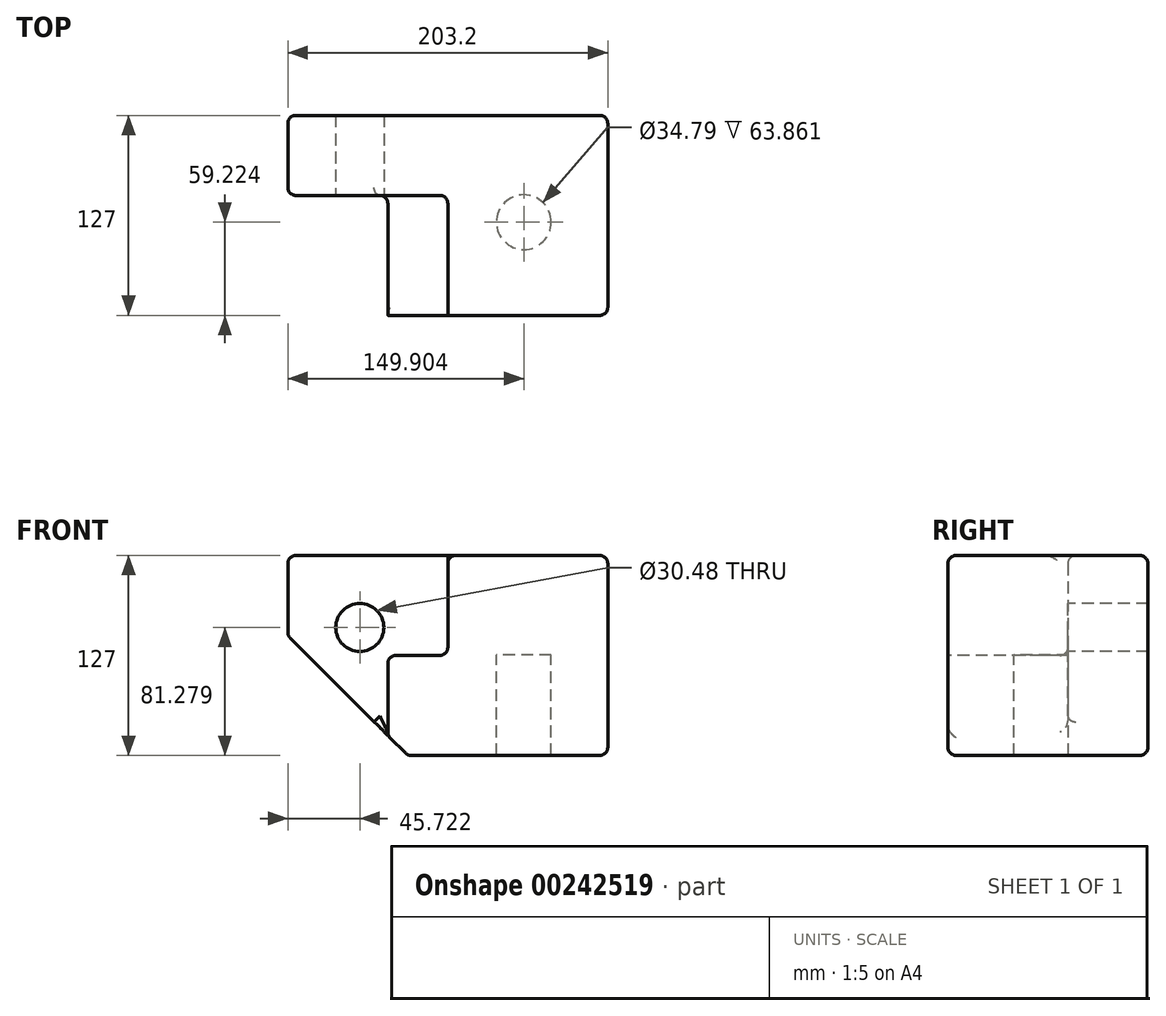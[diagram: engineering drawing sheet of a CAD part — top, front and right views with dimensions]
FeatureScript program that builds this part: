
annotation { "Feature Type Name" : "Feature", "Feature Type Description" : "" }
export const myFeature = defineFeature(function(context is Context, id is Id, definition is map)
    precondition{}
    {
        {
            var Q0;
            Q0=qCreatedBy(makeId("Front.planeOp"),FACE);
            var sketch = newSketch(context, id + "F0", { "sketchPlane" : qUnion([Q0])});
            skLineSegment(sketch, "E0.bottom", {"start": v(-79.8, 63.14) * mm, "end": v(123.4, 63.14) * mm});
            skLineSegment(sketch, "E0.top", {"start": v(-79.8, -63.86) * mm, "end": v(123.4, -63.86) * mm});
            skLineSegment(sketch, "E0.left", {"start": v(-79.8, 63.14) * mm, "end": v(-79.8, -63.86) * mm});
            skLineSegment(sketch, "E0.right", {"start": v(123.4, 63.14) * mm, "end": v(123.4, -63.86) * mm});
            skSolve(sketch);
        }
        {
            var Q0;
            Q0=makeQuery(id+"F0.imprint","IMPRINT",FACE,{"disambiguationData":[TD([[makeQuery(id+"F0.imprint","IMPRINT",EDGE,{"derivedFrom":sQuery(id+"F0.wireOp",EDGE,"E0.bottom")}),-1.0]])]});
            extrude(context, id + "F1", {"entities" : qUnion([Q0]), "depth" : 127 * mm});
        }
        {
            var Q0;
            Q0=makeQuery(id+"F1.opExtrude","CAP_FACE",FACE,{"disambiguationData":[OSD([sQuery(id+"F0.wireOp",EDGE,"E0.bottom"),sQuery(id+"F0.wireOp",EDGE,"E0.top"),sQuery(id+"F0.wireOp",EDGE,"E0.left"),sQuery(id+"F0.wireOp",EDGE,"E0.right")])],"isStart":false});
            var sketch = newSketch(context, id + "F2", { "sketchPlane" : qUnion([Q0])});
            skLineSegment(sketch, "E1", {"start": v(-79.8, 63.14) * mm, "end": v(21.8, 63.14) * mm});
            skLineSegment(sketch, "E2", {"start": v(21.8, 63.14) * mm, "end": v(21.8, -0.36) * mm});
            skLineSegment(sketch, "E3", {"start": v(21.8, -0.36) * mm, "end": v(-16.3, -0.36) * mm});
            skLineSegment(sketch, "E4", {"start": v(-16.3, -0.36) * mm, "end": v(-16.3, -63.86) * mm});
            skLineSegment(sketch, "E5", {"start": v(-16.3, -63.86) * mm, "end": v(-79.8, -63.86) * mm});
            skLineSegment(sketch, "E6", {"start": v(-79.8, -63.86) * mm, "end": v(-79.8, 63.14) * mm});
            skSolve(sketch);
        }
        {
            var Q0;
            Q0=makeQuery(id+"F2.imprint","IMPRINT",FACE,{"disambiguationData":[TD([[makeQuery(id+"F2.imprint","IMPRINT",EDGE,{"derivedFrom":sQuery(id+"F2.wireOp",EDGE,"E1")}),-1.0]])]});
            extrude(context, id + "F3", {"entities" : qUnion([Q0]), "operationType" : NewBodyOperationType.REMOVE, "oppositeDirection" : true, "depth" : 76.2 * mm});
        }
        {
            var Q0;
            Q0=makeQuery(id+"F1.opExtrude","SWEPT_EDGE",EDGE,{"disambiguationData":[OSD([sQuery(id+"F0.wireOp",EDGE,"E0.top"),sQuery(id+"F0.wireOp",EDGE,"E0.left")])]});
            chamfer(context, id + "F4", {"entities" : qUnion([Q0]), "chamferType" : ChamferType.TWO_OFFSETS, "width1" : 76.2 * mm, "oppositeDirection" : false, "width2" : 76.2 * mm, "tangentPropagation" : true});
        }
        {
            var Q0;
            Q0=makeQuery(id+"F1.opExtrude","CAP_EDGE",EDGE,{"disambiguationData":[OSD([sQuery(id+"F0.wireOp",EDGE,"E0.top")])],"isStart":false});
            var Q1;
            {var subQ0=sQuery(id+"F0.wireOp",EDGE,"E0.top");Q1=makeQuery(id+"F4.opChamfer","BLEND_EDGE",EDGE,{"blendedFrom":[makeQuery(id+"F1.opExtrude","SWEPT_EDGE",EDGE,{"disambiguationData":[OSD([subQ0,sQuery(id+"F0.wireOp",EDGE,"E0.left")])]}),makeQuery(id+"F1.opExtrude","SWEPT_FACE",FACE,{"disambiguationData":[OSD([subQ0])]})],"blendedInto":[makeQuery(id+"F1.opExtrude","SWEPT_FACE",FACE,{"disambiguationData":[OSD([subQ0])]})]});}
            var Q2;
            {var subQ0=sQuery(id+"F0.wireOp",EDGE,"E0.left");var subQ1=sQuery(id+"F0.wireOp",EDGE,"E0.top");Q2=makeQuery(id+"F4.opChamfer","BLEND_EDGE",EDGE,{"blendedFrom":[makeQuery(id+"F1.opExtrude","SWEPT_EDGE",EDGE,{"disambiguationData":[OSD([subQ1,subQ0])]}),makeQuery(id+"F1.opExtrude","CAP_FACE",FACE,{"disambiguationData":[OSD([sQuery(id+"F0.wireOp",EDGE,"E0.bottom"),subQ1,subQ0,sQuery(id+"F0.wireOp",EDGE,"E0.right")])],"isStart":false})],"blendedInto":[makeQuery(id+"F1.opExtrude","CAP_FACE",FACE,{"disambiguationData":[OSD([sQuery(id+"F0.wireOp",EDGE,"E0.bottom"),subQ1,subQ0,sQuery(id+"F0.wireOp",EDGE,"E0.right")])],"isStart":false})]});}
            var Q3;
            Q3=makeQuery(id+"F4.opChamfer","BLEND_EDGE",EDGE,{"blendedFrom":[makeQuery(id+"F1.opExtrude","SWEPT_EDGE",EDGE,{"disambiguationData":[OSD([sQuery(id+"F0.wireOp",EDGE,"E0.top"),sQuery(id+"F0.wireOp",EDGE,"E0.left")])]}),makeQuery(id+"F3.boolean.opBoolean","COPY",FACE,{"derivedFrom":makeQuery(id+"F3.opExtrude","SWEPT_FACE",FACE,{"disambiguationData":[OSD([sQuery(id+"F2.wireOp",EDGE,"E4")])]})})],"blendedInto":[makeQuery(id+"F3.boolean.opBoolean","COPY",FACE,{"derivedFrom":makeQuery(id+"F3.opExtrude","SWEPT_FACE",FACE,{"disambiguationData":[OSD([sQuery(id+"F2.wireOp",EDGE,"E4")])]})})]});
            var Q4;
            Q4=makeQuery(id+"F4.opChamfer","BLEND_EDGE",EDGE,{"blendedFrom":[makeQuery(id+"F1.opExtrude","SWEPT_EDGE",EDGE,{"disambiguationData":[OSD([sQuery(id+"F0.wireOp",EDGE,"E0.top"),sQuery(id+"F0.wireOp",EDGE,"E0.left")])]}),makeQuery(id+"F3.boolean.opBoolean","COPY",FACE,{"derivedFrom":makeQuery(id+"F3.opExtrude","CAP_FACE",FACE,{"disambiguationData":[OSD([sQuery(id+"F2.wireOp",EDGE,"E1"),sQuery(id+"F2.wireOp",EDGE,"E2"),sQuery(id+"F2.wireOp",EDGE,"E3"),sQuery(id+"F2.wireOp",EDGE,"E4"),sQuery(id+"F2.wireOp",EDGE,"E5"),sQuery(id+"F2.wireOp",EDGE,"E6")])],"isStart":false})})],"blendedInto":[makeQuery(id+"F3.boolean.opBoolean","COPY",FACE,{"derivedFrom":makeQuery(id+"F3.opExtrude","CAP_FACE",FACE,{"disambiguationData":[OSD([sQuery(id+"F2.wireOp",EDGE,"E1"),sQuery(id+"F2.wireOp",EDGE,"E2"),sQuery(id+"F2.wireOp",EDGE,"E3"),sQuery(id+"F2.wireOp",EDGE,"E4"),sQuery(id+"F2.wireOp",EDGE,"E5"),sQuery(id+"F2.wireOp",EDGE,"E6")])],"isStart":false})})]});
            var Q5;
            {var subQ0=sQuery(id+"F0.wireOp",EDGE,"E0.left");var subQ1=sQuery(id+"F0.wireOp",EDGE,"E0.top");Q5=makeQuery(id+"F4.opChamfer","BLEND_EDGE",EDGE,{"blendedFrom":[makeQuery(id+"F1.opExtrude","SWEPT_EDGE",EDGE,{"disambiguationData":[OSD([subQ1,subQ0])]}),makeQuery(id+"F1.opExtrude","CAP_FACE",FACE,{"disambiguationData":[OSD([sQuery(id+"F0.wireOp",EDGE,"E0.bottom"),subQ1,subQ0,sQuery(id+"F0.wireOp",EDGE,"E0.right")])],"isStart":true})],"blendedInto":[makeQuery(id+"F1.opExtrude","CAP_FACE",FACE,{"disambiguationData":[OSD([sQuery(id+"F0.wireOp",EDGE,"E0.bottom"),subQ1,subQ0,sQuery(id+"F0.wireOp",EDGE,"E0.right")])],"isStart":true})]});}
            var Q6;
            {var subQ0=sQuery(id+"F0.wireOp",EDGE,"E0.left");Q6=makeQuery(id+"F4.opChamfer","BLEND_EDGE",EDGE,{"blendedFrom":[makeQuery(id+"F1.opExtrude","SWEPT_EDGE",EDGE,{"disambiguationData":[OSD([sQuery(id+"F0.wireOp",EDGE,"E0.top"),subQ0])]}),makeQuery(id+"F1.opExtrude","SWEPT_FACE",FACE,{"disambiguationData":[OSD([subQ0])]})],"blendedInto":[makeQuery(id+"F1.opExtrude","SWEPT_FACE",FACE,{"disambiguationData":[OSD([subQ0])]})]});}
            var Q7;
            Q7=makeQuery(id+"F3.boolean.opBoolean","COPY",EDGE,{"derivedFrom":makeQuery(id+"F3.opExtrude","SWEPT_EDGE",EDGE,{"disambiguationData":[OSD([sQuery(id+"F2.wireOp",EDGE,"E3"),sQuery(id+"F2.wireOp",EDGE,"E4")])]})});
            var Q8;
            Q8=makeQuery(id+"F3.boolean.opBoolean","COPY",EDGE,{"derivedFrom":makeQuery(id+"F3.opExtrude","CAP_EDGE",EDGE,{"disambiguationData":[OSD([sQuery(id+"F2.wireOp",EDGE,"E4")])],"isStart":true})});
            var Q9;
            Q9=makeQuery(id+"F3.boolean.opBoolean","COPY",EDGE,{"derivedFrom":makeQuery(id+"F3.opExtrude","CAP_EDGE",EDGE,{"disambiguationData":[OSD([sQuery(id+"F2.wireOp",EDGE,"E4")])],"isStart":false})});
            var Q10;
            Q10=makeQuery(id+"F3.boolean.opBoolean","COPY",FACE,{"derivedFrom":makeQuery(id+"F3.opExtrude","CAP_FACE",FACE,{"disambiguationData":[OSD([sQuery(id+"F2.wireOp",EDGE,"E1"),sQuery(id+"F2.wireOp",EDGE,"E2"),sQuery(id+"F2.wireOp",EDGE,"E3"),sQuery(id+"F2.wireOp",EDGE,"E4"),sQuery(id+"F2.wireOp",EDGE,"E5"),sQuery(id+"F2.wireOp",EDGE,"E6")])],"isStart":false})});
            var Q11;
            Q11=makeQuery(id+"F3.boolean.opBoolean","COPY",EDGE,{"derivedFrom":makeQuery(id+"F3.opExtrude","CAP_EDGE",EDGE,{"disambiguationData":[OSD([sQuery(id+"F2.wireOp",EDGE,"E6")])],"isStart":false})});
            var Q12;
            Q12=makeQuery(id+"F1.opExtrude","CAP_EDGE",EDGE,{"disambiguationData":[OSD([sQuery(id+"F0.wireOp",EDGE,"E0.left")])],"isStart":true});
            var Q13;
            Q13=makeQuery(id+"F1.opExtrude","SWEPT_EDGE",EDGE,{"disambiguationData":[OSD([sQuery(id+"F0.wireOp",EDGE,"E0.bottom"),sQuery(id+"F0.wireOp",EDGE,"E0.left")])]});
            var Q14;
            Q14=makeQuery(id+"F1.opExtrude","CAP_EDGE",EDGE,{"disambiguationData":[OSD([sQuery(id+"F0.wireOp",EDGE,"E0.bottom")])],"isStart":false});
            var Q15;
            Q15=makeQuery(id+"F1.opExtrude","CAP_EDGE",EDGE,{"disambiguationData":[OSD([sQuery(id+"F0.wireOp",EDGE,"E0.right")])],"isStart":false});
            var Q16;
            Q16=makeQuery(id+"F1.opExtrude","SWEPT_EDGE",EDGE,{"disambiguationData":[OSD([sQuery(id+"F0.wireOp",EDGE,"E0.top"),sQuery(id+"F0.wireOp",EDGE,"E0.right")])]});
            var Q17;
            Q17=makeQuery(id+"F1.opExtrude","CAP_EDGE",EDGE,{"disambiguationData":[OSD([sQuery(id+"F0.wireOp",EDGE,"E0.top")])],"isStart":true});
            var Q18;
            Q18=makeQuery(id+"F1.opExtrude","CAP_EDGE",EDGE,{"disambiguationData":[OSD([sQuery(id+"F0.wireOp",EDGE,"E0.bottom")])],"isStart":true});
            var Q19;
            Q19=makeQuery(id+"F1.opExtrude","CAP_EDGE",EDGE,{"disambiguationData":[OSD([sQuery(id+"F0.wireOp",EDGE,"E0.right")])],"isStart":true});
            var Q20;
            Q20=makeQuery(id+"F1.opExtrude","SWEPT_EDGE",EDGE,{"disambiguationData":[OSD([sQuery(id+"F0.wireOp",EDGE,"E0.bottom"),sQuery(id+"F0.wireOp",EDGE,"E0.right")])]});
            var Q21;
            Q21=makeQuery(id+"F3.boolean.opBoolean","COPY",EDGE,{"derivedFrom":makeQuery(id+"F3.opExtrude","CAP_EDGE",EDGE,{"disambiguationData":[OSD([sQuery(id+"F2.wireOp",EDGE,"E2")])],"isStart":true})});
            var Q22;
            Q22=makeQuery(id+"F3.boolean.opBoolean","COPY",EDGE,{"derivedFrom":makeQuery(id+"F3.opExtrude","CAP_EDGE",EDGE,{"disambiguationData":[OSD([sQuery(id+"F2.wireOp",EDGE,"E3")])],"isStart":true})});
            var Q23;
            Q23=makeQuery(id+"F3.boolean.opBoolean","COPY",EDGE,{"derivedFrom":makeQuery(id+"F3.opExtrude","SWEPT_EDGE",EDGE,{"disambiguationData":[OSD([sQuery(id+"F2.wireOp",EDGE,"E2"),sQuery(id+"F2.wireOp",EDGE,"E3")])]})});
            fillet(context, id + "F5", {"entities" : qUnion([Q0, Q1, Q2, Q3, Q4, Q5, Q6, Q7, Q8, Q9, Q10, Q11, Q12, Q13, Q14, Q15, Q16, Q17, Q18, Q19, Q20, Q21, Q22, Q23]), "radius" : 5.08 * mm, "tangentPropagation" : true, "allowEdgeOverflow" : false});
        }
        {
            var Q0;
            Q0=makeQuery(id+"F3.boolean.opBoolean","COPY",FACE,{"derivedFrom":makeQuery(id+"F3.opExtrude","CAP_FACE",FACE,{"disambiguationData":[OSD([sQuery(id+"F2.wireOp",EDGE,"E1"),sQuery(id+"F2.wireOp",EDGE,"E2"),sQuery(id+"F2.wireOp",EDGE,"E3"),sQuery(id+"F2.wireOp",EDGE,"E4"),sQuery(id+"F2.wireOp",EDGE,"E5"),sQuery(id+"F2.wireOp",EDGE,"E6")])],"isStart":false})});
            var sketch = newSketch(context, id + "F6", { "sketchPlane" : qUnion([Q0])});
            skCircle(sketch, "E7", {"center": v(-34.09, 17.42) * mm, "radius": 15.24 * mm});
            skSolve(sketch);
        }
        {
            var Q0;
            Q0=makeQuery(id+"F6.imprint","IMPRINT",FACE,{"disambiguationData":[TD([[makeQuery(id+"F6.imprint","IMPRINT",EDGE,{"derivedFrom":sQuery(id+"F6.wireOp",EDGE,"E7")}),1.0]])]});
            var Q1;
            Q1=makeQuery(id+"F1.opExtrude","CAP_FACE",FACE,{"disambiguationData":[OSD([sQuery(id+"F0.wireOp",EDGE,"E0.bottom"),sQuery(id+"F0.wireOp",EDGE,"E0.top"),sQuery(id+"F0.wireOp",EDGE,"E0.left"),sQuery(id+"F0.wireOp",EDGE,"E0.right")])],"isStart":true});
            extrude(context, id + "F7", {"entities" : qUnion([Q0]), "operationType" : NewBodyOperationType.REMOVE, "endBound" : BoundingType.UP_TO_SURFACE, "oppositeDirection" : true, "endBoundEntityFace" : qUnion([Q1]), "depth" : 25.4 * mm});
        }
        {
            var Q0;
            Q0=qCreatedBy(makeId("Top.planeOp"),FACE);
            var sketch = newSketch(context, id + "F8", { "sketchPlane" : qUnion([Q0])});
            skCircle(sketch, "E8", {"center": v(70.1, -67.78) * mm, "radius": 17.4 * mm});
            skSolve(sketch);
        }
        {
            var Q0;
            Q0 = qSketchRegion(id + "F8", true);
            var Q1;
            Q1=makeQuery(id+"F1.opExtrude","SWEPT_FACE",FACE,{"disambiguationData":[OSD([sQuery(id+"F0.wireOp",EDGE,"E0.top")])]});
            extrude(context, id + "F9", {"entities" : qUnion([Q0]), "operationType" : NewBodyOperationType.REMOVE, "endBound" : BoundingType.UP_TO_SURFACE, "oppositeDirection" : true, "endBoundEntityFace" : qUnion([Q1]), "depth" : 25.4 * mm});
        }
    });
